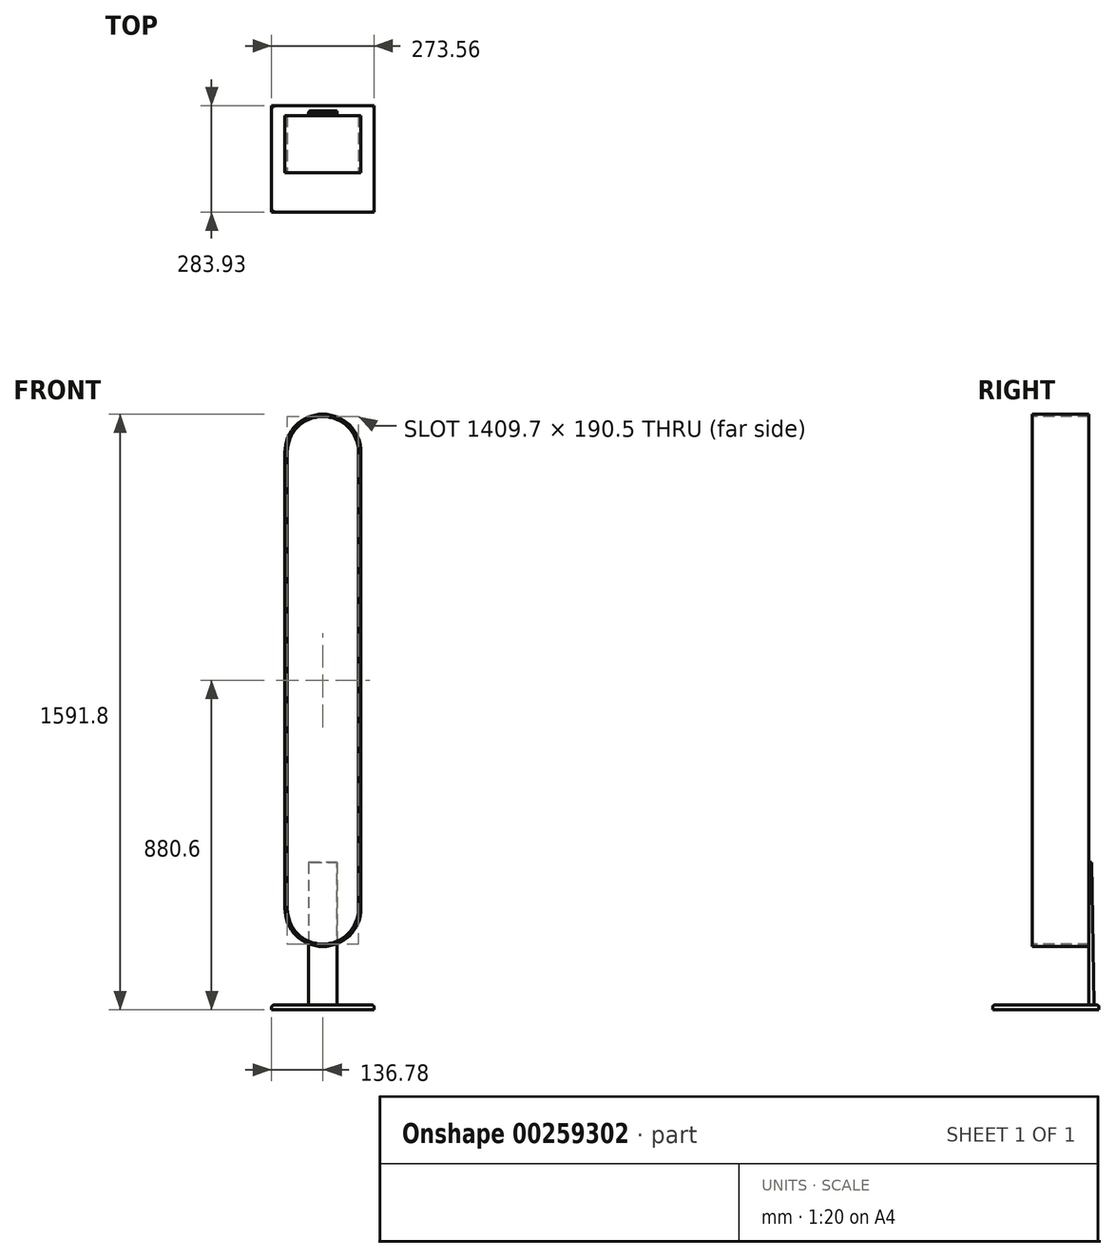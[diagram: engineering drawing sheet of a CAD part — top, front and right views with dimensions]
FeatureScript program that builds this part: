
annotation { "Feature Type Name" : "Feature", "Feature Type Description" : "" }
export const myFeature = defineFeature(function(context is Context, id is Id, definition is map)
    precondition{}
    {
        {
            var Q0;
            Q0=qCreatedBy(makeId("Front.planeOp"),FACE);
            var sketch = newSketch(context, id + "F0", { "sketchPlane" : qUnion([Q0])});
            skLineSegment(sketch, "E0.left", {"start": v(-101.6, 609.6) * mm, "end": v(-101.6, -609.6) * mm});
            skLineSegment(sketch, "E0.right", {"start": v(101.6, 609.6) * mm, "end": v(101.6, -609.6) * mm});
            skPoint(sketch, "E0.middle", {"position": v(0, 0) * mm});
            skArc(sketch, "E1", {"start": v(101.6, 609.6) * mm, "mid": v(0, 711.2) * mm, "end": v(-101.6, 609.6) * mm});
            skArc(sketch, "E2", {"start": v(-101.6, -609.6) * mm, "mid": v(0, -711.2) * mm, "end": v(101.6, -609.6) * mm});
            skLineSegment(sketch, "E3.0", {"start": v(-95.25, 609.6) * mm, "end": v(-95.25, -609.6) * mm});
            skArc(sketch, "E3.1", {"start": v(95.25, 609.6) * mm, "mid": v(0, 704.85) * mm, "end": v(-95.25, 609.6) * mm});
            skLineSegment(sketch, "E3.2", {"start": v(95.25, 609.6) * mm, "end": v(95.25, -609.6) * mm});
            skArc(sketch, "E3.3", {"start": v(-95.25, -609.6) * mm, "mid": v(0, -704.85) * mm, "end": v(95.25, -609.6) * mm});
            skSolve(sketch);
        }
        {
            var Q0;
            Q0=makeQuery(id+"F0.imprint","IMPRINT",FACE,{"disambiguationData":[TD([[makeQuery(id+"F0.imprint","IMPRINT",EDGE,{"derivedFrom":sQuery(id+"F0.wireOp",EDGE,"E0.left")}),1.0]])]});
            extrude(context, id + "F1", {"entities" : qUnion([Q0]), "oppositeDirection" : true, "depth" : 152.4 * mm});
        }
        {
            var Q0;
            Q0=makeQuery(id+"F1.opExtrude","CAP_FACE",FACE,{"disambiguationData":[OSD([sQuery(id+"F0.wireOp",EDGE,"E0.left"),sQuery(id+"F0.wireOp",EDGE,"E0.right"),sQuery(id+"F0.wireOp",EDGE,"E1"),sQuery(id+"F0.wireOp",EDGE,"E2"),sQuery(id+"F0.wireOp",EDGE,"E3.0"),sQuery(id+"F0.wireOp",EDGE,"E3.1"),sQuery(id+"F0.wireOp",EDGE,"E3.2"),sQuery(id+"F0.wireOp",EDGE,"E3.3")])],"isStart":true});
            var sketch = newSketch(context, id + "F2", { "sketchPlane" : qUnion([Q0])});
            skSolve(sketch);
        }
        {
            var Q0;
            Q0=makeQuery(id+"F2.imprint","IMPRINT",FACE,{"disambiguationData":[TD([[makeQuery(id+"F2.imprint","IMPRINT",EDGE,{"derivedFrom":makeQuery(id+"F1.opExtrude","CAP_EDGE",EDGE,{"disambiguationData":[OSD([sQuery(id+"F0.wireOp",EDGE,"E3.0")])],"isStart":true})}),1.0]])]});
            extrude(context, id + "F3", {"entities" : qUnion([Q0]), "oppositeDirection" : true, "depth" : 152.4 * mm});
        }
        {
            var Q0;
            Q0=makeQuery(id+"F3.opExtrude","CAP_FACE",FACE,{"disambiguationData":[OSD([sQuery(id+"F0.wireOp",EDGE,"E3.0"),sQuery(id+"F0.wireOp",EDGE,"E3.1"),sQuery(id+"F0.wireOp",EDGE,"E3.2"),sQuery(id+"F0.wireOp",EDGE,"E3.3")])],"isStart":false});
            var sketch = newSketch(context, id + "F4", { "sketchPlane" : qUnion([Q0])});
            skLineSegment(sketch, "E4.top", {"start": v(-38.1, -867.9) * mm, "end": v(38.1, -867.9) * mm});
            skLineSegment(sketch, "E4.left", {"start": v(-38.1, -486.9) * mm, "end": v(-38.1, -867.9) * mm});
            skLineSegment(sketch, "E4.right", {"start": v(38.1, -486.9) * mm, "end": v(38.1, -867.9) * mm});
            skPoint(sketch, "E4.middle", {"position": v(0, -609.6) * mm});
            skLineSegment(sketch, "E5", {"start": v(-38.1, -486.9) * mm, "end": v(38.1, -486.9) * mm});
            skPoint(sketch, "E4.bottom.start.orphan", {"position": v(-38.1, -351.3) * mm});
            skPoint(sketch, "E6.orphan", {"position": v(38.1, -351.3) * mm});
            skSolve(sketch);
        }
        {
            var Q0;
            Q0 = qSketchRegion(id + "F4", true);
            extrude(context, id + "F5", {"entities" : qUnion([Q0]), "depth" : 12.7 * mm});
        }
        {
            var Q0;
            Q0=makeQuery(id+"F5.opExtrude","SWEPT_FACE",FACE,{"disambiguationData":[OSD([sQuery(id+"F4.wireOp",EDGE,"E4.left")])]});
            var sketch = newSketch(context, id + "F6", { "sketchPlane" : qUnion([Q0])});
            skLineSegment(sketch, "E7", {"start": v(165.1, -867.9) * mm, "end": v(158.75, -486.9) * mm});
            skLineSegment(sketch, "E8", {"start": v(158.75, -486.9) * mm, "end": v(165.1, -486.9) * mm});
            skLineSegment(sketch, "E9", {"start": v(165.1, -486.9) * mm, "end": v(165.1, -867.9) * mm});
            skSolve(sketch);
        }
        {
            var Q0;
            Q0 = qSketchRegion(id + "F6", true);
            extrude(context, id + "F7", {"entities" : qUnion([Q0]), "operationType" : NewBodyOperationType.REMOVE, "endBound" : BoundingType.THROUGH_ALL, "oppositeDirection" : true, "depth" : 25.4 * mm});
        }
        {
            var Q0;
            Q0=makeQuery(id+"F7.boolean.opBoolean","COPY",EDGE,{"derivedFrom":makeQuery(id+"F7.opExtrude","CAP_EDGE",EDGE,{"disambiguationData":[OSD([sQuery(id+"F6.wireOp",EDGE,"E7")])],"isStart":true})});
            var Q1;
            Q1=makeQuery(id+"F7.boolean.opBoolean","INTERSECT",EDGE,{"derivedFrom":[makeQuery(id+"F5.opExtrude","SWEPT_FACE",FACE,{"disambiguationData":[OSD([sQuery(id+"F4.wireOp",EDGE,"E4.right")])]}),makeQuery(id+"F7.opExtrude","SWEPT_FACE",FACE,{"disambiguationData":[OSD([sQuery(id+"F6.wireOp",EDGE,"E7")])]})]});
            var Q2;
            Q2=makeQuery(id+"F7.boolean.opBoolean","COPY",EDGE,{"derivedFrom":makeQuery(id+"F7.opExtrude","SWEPT_EDGE",EDGE,{"disambiguationData":[OSD([sQuery(id+"F4.wireOp",EDGE,"E4.left"),sQuery(id+"F4.wireOp",EDGE,"E5"),sQuery(id+"F6.wireOp",EDGE,"E7"),sQuery(id+"F6.wireOp",EDGE,"E8")])]})});
            fillet(context, id + "F8", {"entities" : qUnion([Q0, Q1, Q2]), "radius" : 5.08 * mm, "tangentPropagation" : true, "allowEdgeOverflow" : false});
        }
        {
            var Q0;
            Q0=makeQuery(id+"F5.opExtrude","SWEPT_FACE",FACE,{"disambiguationData":[OSD([sQuery(id+"F4.wireOp",EDGE,"E4.top")])]});
            var sketch = newSketch(context, id + "F9", { "sketchPlane" : qUnion([Q0])});
            skLineSegment(sketch, "E10.bottom", {"start": v(-136.78, 105.26) * mm, "end": v(136.78, 105.26) * mm});
            skLineSegment(sketch, "E10.left", {"start": v(-136.78, 105.26) * mm, "end": v(-136.78, -178.67) * mm});
            skLineSegment(sketch, "E10.right", {"start": v(136.78, 105.26) * mm, "end": v(136.78, -178.67) * mm});
            skPoint(sketch, "E10.middle", {"position": v(0, -152.4) * mm});
            skLineSegment(sketch, "E11", {"start": v(136.78, -178.67) * mm, "end": v(-136.78, -178.67) * mm});
            skPoint(sketch, "E10.top.start.orphan", {"position": v(-136.78, -410.06) * mm});
            skPoint(sketch, "E12.orphan", {"position": v(136.78, -410.06) * mm});
            skSolve(sketch);
        }
        {
            var Q0;
            Q0 = qSketchRegion(id + "F9", true);
            extrude(context, id + "F10", {"entities" : qUnion([Q0]), "operationType" : NewBodyOperationType.ADD, "depth" : 12.7 * mm});
        }
        {
            var Q0;
            Q0=makeQuery(id+"F10.opExtrude","CAP_EDGE",EDGE,{"disambiguationData":[OSD([sQuery(id+"F9.wireOp",EDGE,"E10.left")])],"isStart":true});
            var Q1;
            Q1=makeQuery(id+"F10.opExtrude","CAP_EDGE",EDGE,{"disambiguationData":[OSD([sQuery(id+"F9.wireOp",EDGE,"E10.bottom")])],"isStart":true});
            var Q2;
            Q2=makeQuery(id+"F10.opExtrude","CAP_EDGE",EDGE,{"disambiguationData":[OSD([sQuery(id+"F9.wireOp",EDGE,"E10.right")])],"isStart":true});
            var Q3;
            Q3=makeQuery(id+"F10.opExtrude","CAP_EDGE",EDGE,{"disambiguationData":[OSD([sQuery(id+"F9.wireOp",EDGE,"E11")])],"isStart":true});
            fillet(context, id + "F11", {"entities" : qUnion([Q0, Q1, Q2, Q3]), "radius" : 5.08 * mm, "tangentPropagation" : true, "allowEdgeOverflow" : false});
        }
    });
